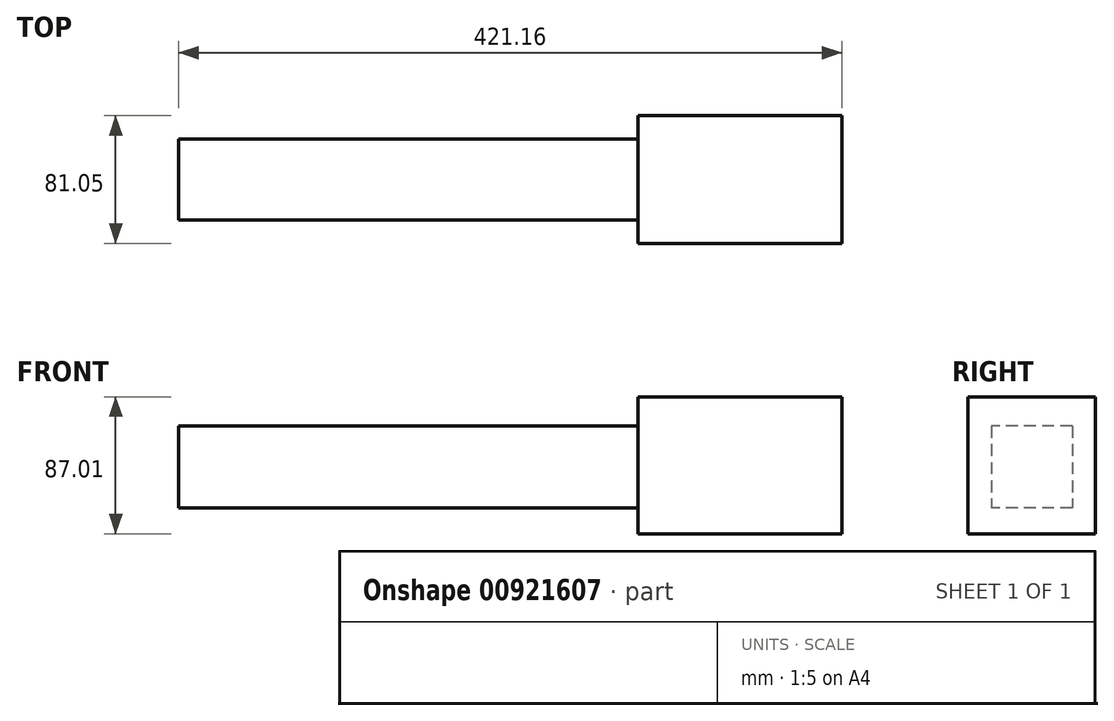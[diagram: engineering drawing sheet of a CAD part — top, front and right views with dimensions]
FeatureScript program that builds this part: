
annotation { "Feature Type Name" : "Feature", "Feature Type Description" : "" }
export const myFeature = defineFeature(function(context is Context, id is Id, definition is map)
    precondition{}
    {
        {
            var Q0;
            Q0=qCreatedBy(makeId("Right.planeOp"),FACE);
            var sketch = newSketch(context, id + "F0", { "sketchPlane" : qUnion([Q0])});
            skLineSegment(sketch, "E0.bottom", {"start": v(81.05, 87) * mm, "end": v(0, 87) * mm});
            skLineSegment(sketch, "E0.top", {"start": v(81.05, 0) * mm, "end": v(0, 0) * mm});
            skLineSegment(sketch, "E0.left", {"start": v(81.05, 87) * mm, "end": v(81.05, 0) * mm});
            skLineSegment(sketch, "E0.right", {"start": v(0, 87) * mm, "end": v(0, 0) * mm});
            skLineSegment(sketch, "E1.bottom", {"start": v(0, 0) * mm, "end": v(-95.66, 0) * mm});
            skLineSegment(sketch, "E1.top", {"start": v(0, -96.83) * mm, "end": v(-95.66, -96.83) * mm});
            skLineSegment(sketch, "E1.left", {"start": v(0, 0) * mm, "end": v(0, -96.83) * mm});
            skLineSegment(sketch, "E1.right", {"start": v(-95.66, 0) * mm, "end": v(-95.66, -96.83) * mm});
            skSolve(sketch);
        }
        {
            var Q0;
            Q0=makeQuery(id+"F0.imprint","IMPRINT",FACE,{"disambiguationData":[TD([[makeQuery(id+"F0.imprint","IMPRINT",EDGE,{"derivedFrom":sQuery(id+"F0.wireOp",EDGE,"E0.bottom")}),1.0]])]});
            extrude(context, id + "F1", {"entities" : qUnion([Q0]), "depth" : 129.56 * mm, "offsetDistance" : 25.4 * mm});
        }
        {
            var Q0;
            Q0=makeQuery(id+"F1.opExtrude","CAP_FACE",FACE,{"disambiguationData":[OSD([sQuery(id+"F0.wireOp",EDGE,"E0.bottom"),sQuery(id+"F0.wireOp",EDGE,"E0.top"),sQuery(id+"F0.wireOp",EDGE,"E0.left"),sQuery(id+"F0.wireOp",EDGE,"E0.right")])],"isStart":false});
            var sketch = newSketch(context, id + "F2", { "sketchPlane" : qUnion([Q0])});
            skLineSegment(sketch, "E2.bottom", {"start": v(66.27, 68.41) * mm, "end": v(14.91, 68.41) * mm});
            skLineSegment(sketch, "E2.top", {"start": v(66.27, 16.55) * mm, "end": v(14.91, 16.55) * mm});
            skLineSegment(sketch, "E2.left", {"start": v(66.27, 68.41) * mm, "end": v(66.27, 16.55) * mm});
            skLineSegment(sketch, "E2.right", {"start": v(14.91, 68.41) * mm, "end": v(14.91, 16.55) * mm});
            skSolve(sketch);
        }
        {
            var Q0;
            Q0=makeQuery(id+"F2.imprint","IMPRINT",FACE,{"disambiguationData":[TD([[makeQuery(id+"F2.imprint","IMPRINT",EDGE,{"derivedFrom":sQuery(id+"F2.wireOp",EDGE,"E2.bottom")}),1.0]])]});
            extrude(context, id + "F3", {"entities" : qUnion([Q0]), "operationType" : NewBodyOperationType.ADD, "oppositeDirection" : true, "depth" : 421.16 * mm, "offsetDistance" : 25.4 * mm});
        }
    });
